# Revit family: Lavatory-TOTO-Contemporary-Soiree-LPT960
name_source: partatom
category: Plumbing Fixtures
revit_build: Autodesk Revit Architecture 2013 (Build: 20130531_2115(x64)
units: mm (PartAtom-declared; Revit-internal decimal feet)

## types (1)
- LPT960
    04 CSI = 22 42 16
    95 CSI = 15410
    ADA Compliant = No
    Assembly Code = D2010310
    Basin Depth = 1' - 0 1/4"
    Basin Width = 1' - 11 1/8"
    CAD Drawing URL = http://assets.totousa.com
    Certifications = IAPMO(cUPC), State of Massachusetts, City of Los Angeles, and others
    Code Compliance = UPC, IPC, NSPC, NPC Canada, and others
    Cold Water Connection Radius = 0' - 0 3/8"
    Cold Water Connector = Cold Water Connection
    Color Availability = #01 Cotton,#03 Bone,#11 Colonial White,#12 Sedona Beige,#51 Ebony
    Default Elevation = 4' - 0"
    Depth = 1' - 7 5/8"
    Finish = Vitreous China - TOTO - 01 Cotton
    Height = 2' - 10"
    Hot Water Connection Radius = 0' - 0 3/8"
    Hot Water Connector = Hot Water Connection
    Industry Standards = Meets and exceeds ASME A112.19.2/CSA B45.1
    Manufacturer = TOTO USA, Inc.
    Manufacturer Fax = (770) 282-0002
    Material = Vitreous china
    Model = LPT960
    Sanitary Connector = Sanitary Connection
    SanoGloss Available = No
    Series = Soirée
    Shipping Weight = 52.00 lb
    Sink Type = Lavatory
    Spec Sheet URL = http://assets.totousa.com
    Style = Contemporary
    Subcategory = Lavatories
    Toto BIM Number = BM-00348
    URL = http://www.totousa.com
    Warranty = One Year Limited Warranty
    Warranty URL = http://www.totousa.com
    Waste Connection NPT Radius = 0' - 0 5/8"
    Width = 2' - 5 1/2"
    ecoScorecard Product Page = http://toto.ecoscorecard.com
    ecoScorecard_data = http://toto.ecoscorecard.com

## geometry (parser evidence)
native form markers: Blend x4, Sweep x8
no freeform markers — native parametric forms only
